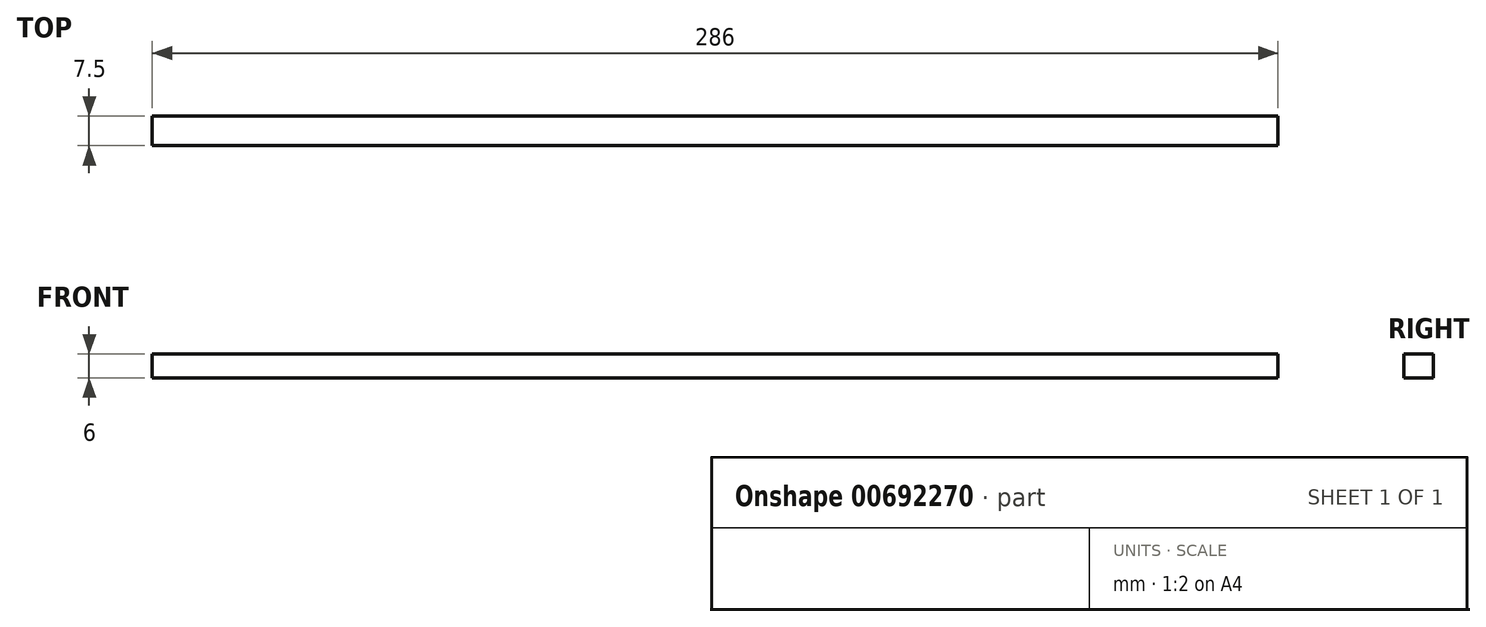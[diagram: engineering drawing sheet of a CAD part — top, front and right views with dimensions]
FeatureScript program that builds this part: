
annotation { "Feature Type Name" : "Feature", "Feature Type Description" : "" }
export const myFeature = defineFeature(function(context is Context, id is Id, definition is map)
    precondition{}
    {
        {
            var Q0;
            Q0=qCreatedBy(makeId("Top.planeOp"),FACE);
            var sketch = newSketch(context, id + "F0", { "sketchPlane" : qUnion([Q0])});
            skLineSegment(sketch, "E0.bottom", {"start": v(0, 0) * mm, "end": v(286, 0) * mm});
            skLineSegment(sketch, "E0.top", {"start": v(0, 7.5) * mm, "end": v(286, 7.5) * mm});
            skLineSegment(sketch, "E0.left", {"start": v(0, 0) * mm, "end": v(0, 7.5) * mm});
            skLineSegment(sketch, "E0.right", {"start": v(286, 0) * mm, "end": v(286, 7.5) * mm});
            skSolve(sketch);
        }
        {
            var Q0;
            Q0 = qSketchRegion(id + "F0", true);
            extrude(context, id + "F1", {"entities" : qUnion([Q0]), "depth" : 6 * mm, "offsetDistance" : 25.4 * mm});
        }
    });
